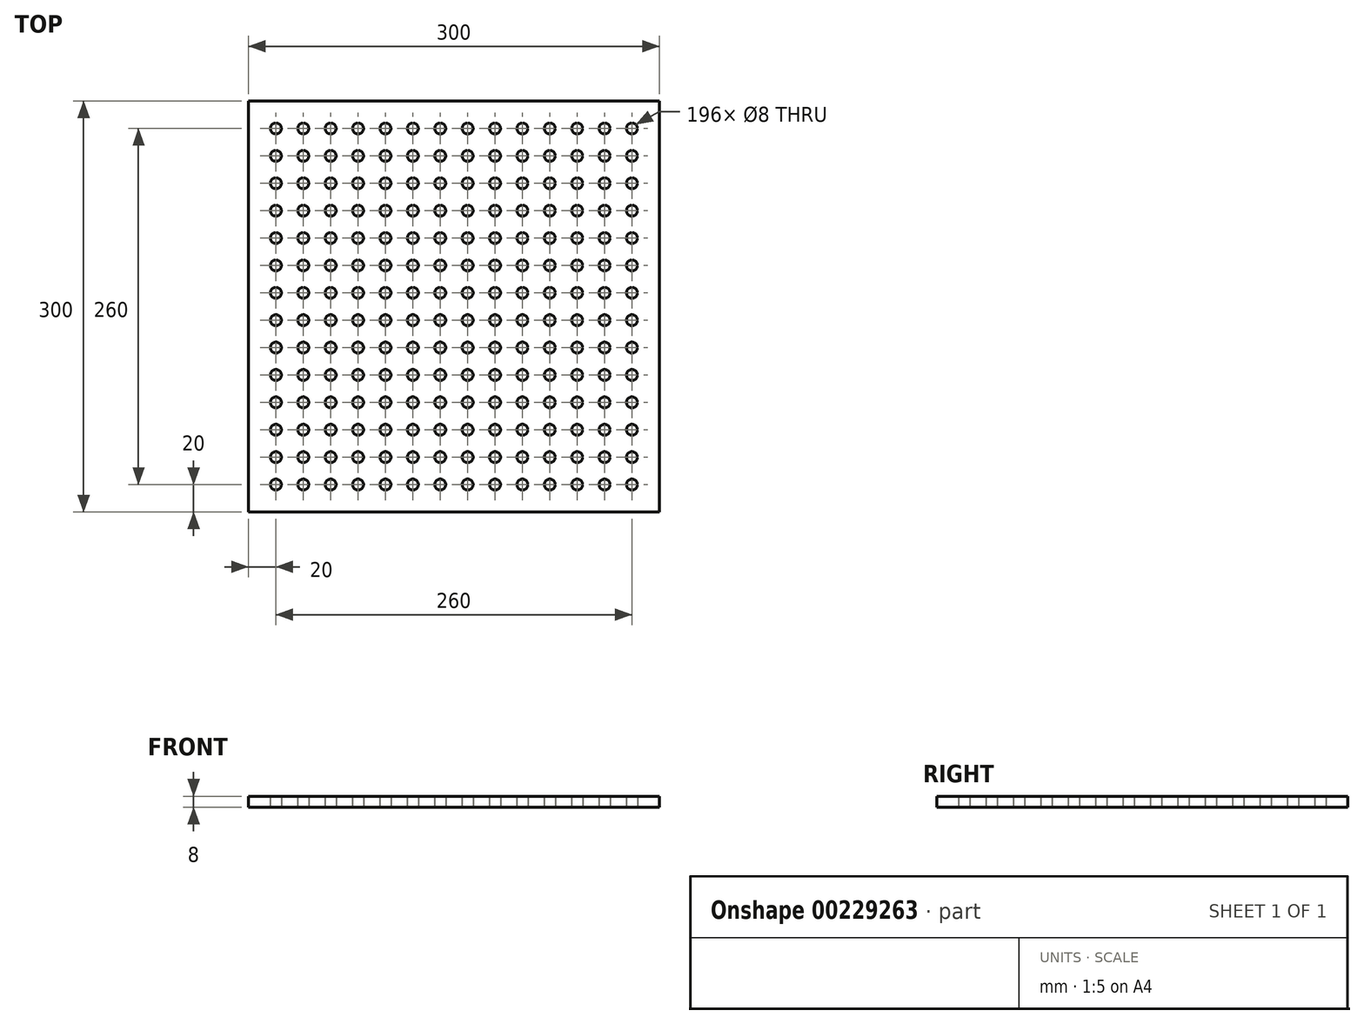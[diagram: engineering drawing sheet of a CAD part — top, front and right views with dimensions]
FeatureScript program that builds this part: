
annotation { "Feature Type Name" : "Feature", "Feature Type Description" : "" }
export const myFeature = defineFeature(function(context is Context, id is Id, definition is map)
    precondition{}
    {
        {
            var Q0;
            Q0=qCreatedBy(makeId("Top.planeOp"),FACE);
            var sketch = newSketch(context, id + "F0", { "sketchPlane" : qUnion([Q0])});
            skLineSegment(sketch, "E0.bottom", {"start": v(-150, 150) * mm, "end": v(150, 150) * mm});
            skLineSegment(sketch, "E0.top", {"start": v(-150, -150) * mm, "end": v(150, -150) * mm});
            skLineSegment(sketch, "E0.left", {"start": v(-150, 150) * mm, "end": v(-150, -150) * mm});
            skLineSegment(sketch, "E0.right", {"start": v(150, 150) * mm, "end": v(150, -150) * mm});
            skPoint(sketch, "E0.middle", {"position": v(0, 0) * mm});
            skCircle(sketch, "E1", {"center": v(-130, -130) * mm, "radius": 4 * mm});
            skCircle(sketch, "E2.0.1.0", {"center": v(-130, -110) * mm, "radius": 4 * mm});
            skCircle(sketch, "E2.0.2.0", {"center": v(-130, -90) * mm, "radius": 4 * mm});
            skCircle(sketch, "E2.0.3.0", {"center": v(-130, -70) * mm, "radius": 4 * mm});
            skCircle(sketch, "E2.0.4.0", {"center": v(-130, -50) * mm, "radius": 4 * mm});
            skCircle(sketch, "E2.0.5.0", {"center": v(-130, -30) * mm, "radius": 4 * mm});
            skCircle(sketch, "E2.0.6.0", {"center": v(-130, -10) * mm, "radius": 4 * mm});
            skCircle(sketch, "E2.0.7.0", {"center": v(-130, 10) * mm, "radius": 4 * mm});
            skCircle(sketch, "E2.0.8.0", {"center": v(-130, 30) * mm, "radius": 4 * mm});
            skCircle(sketch, "E2.0.9.0", {"center": v(-130, 50) * mm, "radius": 4 * mm});
            skCircle(sketch, "E2.0.10.0", {"center": v(-130, 70) * mm, "radius": 4 * mm});
            skCircle(sketch, "E2.0.11.0", {"center": v(-130, 90) * mm, "radius": 4 * mm});
            skCircle(sketch, "E2.0.12.0", {"center": v(-130, 110) * mm, "radius": 4 * mm});
            skCircle(sketch, "E2.0.13.0", {"center": v(-130, 130) * mm, "radius": 4 * mm});
            skCircle(sketch, "E2.1.0.0", {"center": v(-110, -130) * mm, "radius": 4 * mm});
            skCircle(sketch, "E2.1.1.0", {"center": v(-110, -110) * mm, "radius": 4 * mm});
            skCircle(sketch, "E2.1.2.0", {"center": v(-110, -90) * mm, "radius": 4 * mm});
            skCircle(sketch, "E2.1.3.0", {"center": v(-110, -70) * mm, "radius": 4 * mm});
            skCircle(sketch, "E2.1.4.0", {"center": v(-110, -50) * mm, "radius": 4 * mm});
            skCircle(sketch, "E2.1.5.0", {"center": v(-110, -30) * mm, "radius": 4 * mm});
            skCircle(sketch, "E2.1.6.0", {"center": v(-110, -10) * mm, "radius": 4 * mm});
            skCircle(sketch, "E2.1.7.0", {"center": v(-110, 10) * mm, "radius": 4 * mm});
            skCircle(sketch, "E2.1.8.0", {"center": v(-110, 30) * mm, "radius": 4 * mm});
            skCircle(sketch, "E2.1.9.0", {"center": v(-110, 50) * mm, "radius": 4 * mm});
            skCircle(sketch, "E2.1.10.0", {"center": v(-110, 70) * mm, "radius": 4 * mm});
            skCircle(sketch, "E2.1.11.0", {"center": v(-110, 90) * mm, "radius": 4 * mm});
            skCircle(sketch, "E2.1.12.0", {"center": v(-110, 110) * mm, "radius": 4 * mm});
            skCircle(sketch, "E2.1.13.0", {"center": v(-110, 130) * mm, "radius": 4 * mm});
            skCircle(sketch, "E2.2.0.0", {"center": v(-90, -130) * mm, "radius": 4 * mm});
            skCircle(sketch, "E2.2.1.0", {"center": v(-90, -110) * mm, "radius": 4 * mm});
            skCircle(sketch, "E2.2.2.0", {"center": v(-90, -90) * mm, "radius": 4 * mm});
            skCircle(sketch, "E2.2.3.0", {"center": v(-90, -70) * mm, "radius": 4 * mm});
            skCircle(sketch, "E2.2.4.0", {"center": v(-90, -50) * mm, "radius": 4 * mm});
            skCircle(sketch, "E2.2.5.0", {"center": v(-90, -30) * mm, "radius": 4 * mm});
            skCircle(sketch, "E2.2.6.0", {"center": v(-90, -10) * mm, "radius": 4 * mm});
            skCircle(sketch, "E2.2.7.0", {"center": v(-90, 10) * mm, "radius": 4 * mm});
            skCircle(sketch, "E2.2.8.0", {"center": v(-90, 30) * mm, "radius": 4 * mm});
            skCircle(sketch, "E2.2.9.0", {"center": v(-90, 50) * mm, "radius": 4 * mm});
            skCircle(sketch, "E2.2.10.0", {"center": v(-90, 70) * mm, "radius": 4 * mm});
            skCircle(sketch, "E2.2.11.0", {"center": v(-90, 90) * mm, "radius": 4 * mm});
            skCircle(sketch, "E2.2.12.0", {"center": v(-90, 110) * mm, "radius": 4 * mm});
            skCircle(sketch, "E2.2.13.0", {"center": v(-90, 130) * mm, "radius": 4 * mm});
            skCircle(sketch, "E2.3.0.0", {"center": v(-70, -130) * mm, "radius": 4 * mm});
            skCircle(sketch, "E2.3.1.0", {"center": v(-70, -110) * mm, "radius": 4 * mm});
            skCircle(sketch, "E2.3.2.0", {"center": v(-70, -90) * mm, "radius": 4 * mm});
            skCircle(sketch, "E2.3.3.0", {"center": v(-70, -70) * mm, "radius": 4 * mm});
            skCircle(sketch, "E2.3.4.0", {"center": v(-70, -50) * mm, "radius": 4 * mm});
            skCircle(sketch, "E2.3.5.0", {"center": v(-70, -30) * mm, "radius": 4 * mm});
            skCircle(sketch, "E2.3.6.0", {"center": v(-70, -10) * mm, "radius": 4 * mm});
            skCircle(sketch, "E2.3.7.0", {"center": v(-70, 10) * mm, "radius": 4 * mm});
            skCircle(sketch, "E2.3.8.0", {"center": v(-70, 30) * mm, "radius": 4 * mm});
            skCircle(sketch, "E2.3.9.0", {"center": v(-70, 50) * mm, "radius": 4 * mm});
            skCircle(sketch, "E2.3.10.0", {"center": v(-70, 70) * mm, "radius": 4 * mm});
            skCircle(sketch, "E2.3.11.0", {"center": v(-70, 90) * mm, "radius": 4 * mm});
            skCircle(sketch, "E2.3.12.0", {"center": v(-70, 110) * mm, "radius": 4 * mm});
            skCircle(sketch, "E2.3.13.0", {"center": v(-70, 130) * mm, "radius": 4 * mm});
            skCircle(sketch, "E2.4.0.0", {"center": v(-50, -130) * mm, "radius": 4 * mm});
            skCircle(sketch, "E2.4.1.0", {"center": v(-50, -110) * mm, "radius": 4 * mm});
            skCircle(sketch, "E2.4.2.0", {"center": v(-50, -90) * mm, "radius": 4 * mm});
            skCircle(sketch, "E2.4.3.0", {"center": v(-50, -70) * mm, "radius": 4 * mm});
            skCircle(sketch, "E2.4.4.0", {"center": v(-50, -50) * mm, "radius": 4 * mm});
            skCircle(sketch, "E2.4.5.0", {"center": v(-50, -30) * mm, "radius": 4 * mm});
            skCircle(sketch, "E2.4.6.0", {"center": v(-50, -10) * mm, "radius": 4 * mm});
            skCircle(sketch, "E2.4.7.0", {"center": v(-50, 10) * mm, "radius": 4 * mm});
            skCircle(sketch, "E2.4.8.0", {"center": v(-50, 30) * mm, "radius": 4 * mm});
            skCircle(sketch, "E2.4.9.0", {"center": v(-50, 50) * mm, "radius": 4 * mm});
            skCircle(sketch, "E2.4.10.0", {"center": v(-50, 70) * mm, "radius": 4 * mm});
            skCircle(sketch, "E2.4.11.0", {"center": v(-50, 90) * mm, "radius": 4 * mm});
            skCircle(sketch, "E2.4.12.0", {"center": v(-50, 110) * mm, "radius": 4 * mm});
            skCircle(sketch, "E2.4.13.0", {"center": v(-50, 130) * mm, "radius": 4 * mm});
            skCircle(sketch, "E2.5.0.0", {"center": v(-30, -130) * mm, "radius": 4 * mm});
            skCircle(sketch, "E2.5.1.0", {"center": v(-30, -110) * mm, "radius": 4 * mm});
            skCircle(sketch, "E2.5.2.0", {"center": v(-30, -90) * mm, "radius": 4 * mm});
            skCircle(sketch, "E2.5.3.0", {"center": v(-30, -70) * mm, "radius": 4 * mm});
            skCircle(sketch, "E2.5.4.0", {"center": v(-30, -50) * mm, "radius": 4 * mm});
            skCircle(sketch, "E2.5.5.0", {"center": v(-30, -30) * mm, "radius": 4 * mm});
            skCircle(sketch, "E2.5.6.0", {"center": v(-30, -10) * mm, "radius": 4 * mm});
            skCircle(sketch, "E2.5.7.0", {"center": v(-30, 10) * mm, "radius": 4 * mm});
            skCircle(sketch, "E2.5.8.0", {"center": v(-30, 30) * mm, "radius": 4 * mm});
            skCircle(sketch, "E2.5.9.0", {"center": v(-30, 50) * mm, "radius": 4 * mm});
            skCircle(sketch, "E2.5.10.0", {"center": v(-30, 70) * mm, "radius": 4 * mm});
            skCircle(sketch, "E2.5.11.0", {"center": v(-30, 90) * mm, "radius": 4 * mm});
            skCircle(sketch, "E2.5.12.0", {"center": v(-30, 110) * mm, "radius": 4 * mm});
            skCircle(sketch, "E2.5.13.0", {"center": v(-30, 130) * mm, "radius": 4 * mm});
            skCircle(sketch, "E2.6.0.0", {"center": v(-10, -130) * mm, "radius": 4 * mm});
            skCircle(sketch, "E2.6.1.0", {"center": v(-10, -110) * mm, "radius": 4 * mm});
            skCircle(sketch, "E2.6.2.0", {"center": v(-10, -90) * mm, "radius": 4 * mm});
            skCircle(sketch, "E2.6.3.0", {"center": v(-10, -70) * mm, "radius": 4 * mm});
            skCircle(sketch, "E2.6.4.0", {"center": v(-10, -50) * mm, "radius": 4 * mm});
            skCircle(sketch, "E2.6.5.0", {"center": v(-10, -30) * mm, "radius": 4 * mm});
            skCircle(sketch, "E2.6.6.0", {"center": v(-10, -10) * mm, "radius": 4 * mm});
            skCircle(sketch, "E2.6.7.0", {"center": v(-10, 10) * mm, "radius": 4 * mm});
            skCircle(sketch, "E2.6.8.0", {"center": v(-10, 30) * mm, "radius": 4 * mm});
            skCircle(sketch, "E2.6.9.0", {"center": v(-10, 50) * mm, "radius": 4 * mm});
            skCircle(sketch, "E2.6.10.0", {"center": v(-10, 70) * mm, "radius": 4 * mm});
            skCircle(sketch, "E2.6.11.0", {"center": v(-10, 90) * mm, "radius": 4 * mm});
            skCircle(sketch, "E2.6.12.0", {"center": v(-10, 110) * mm, "radius": 4 * mm});
            skCircle(sketch, "E2.6.13.0", {"center": v(-10, 130) * mm, "radius": 4 * mm});
            skCircle(sketch, "E2.7.0.0", {"center": v(10, -130) * mm, "radius": 4 * mm});
            skCircle(sketch, "E2.7.1.0", {"center": v(10, -110) * mm, "radius": 4 * mm});
            skCircle(sketch, "E2.7.2.0", {"center": v(10, -90) * mm, "radius": 4 * mm});
            skCircle(sketch, "E2.7.3.0", {"center": v(10, -70) * mm, "radius": 4 * mm});
            skCircle(sketch, "E2.7.4.0", {"center": v(10, -50) * mm, "radius": 4 * mm});
            skCircle(sketch, "E2.7.5.0", {"center": v(10, -30) * mm, "radius": 4 * mm});
            skCircle(sketch, "E2.7.6.0", {"center": v(10, -10) * mm, "radius": 4 * mm});
            skCircle(sketch, "E2.7.7.0", {"center": v(10, 10) * mm, "radius": 4 * mm});
            skCircle(sketch, "E2.7.8.0", {"center": v(10, 30) * mm, "radius": 4 * mm});
            skCircle(sketch, "E2.7.9.0", {"center": v(10, 50) * mm, "radius": 4 * mm});
            skCircle(sketch, "E2.7.10.0", {"center": v(10, 70) * mm, "radius": 4 * mm});
            skCircle(sketch, "E2.7.11.0", {"center": v(10, 90) * mm, "radius": 4 * mm});
            skCircle(sketch, "E2.7.12.0", {"center": v(10, 110) * mm, "radius": 4 * mm});
            skCircle(sketch, "E2.7.13.0", {"center": v(10, 130) * mm, "radius": 4 * mm});
            skCircle(sketch, "E2.8.0.0", {"center": v(30, -130) * mm, "radius": 4 * mm});
            skCircle(sketch, "E2.8.1.0", {"center": v(30, -110) * mm, "radius": 4 * mm});
            skCircle(sketch, "E2.8.2.0", {"center": v(30, -90) * mm, "radius": 4 * mm});
            skCircle(sketch, "E2.8.3.0", {"center": v(30, -70) * mm, "radius": 4 * mm});
            skCircle(sketch, "E2.8.4.0", {"center": v(30, -50) * mm, "radius": 4 * mm});
            skCircle(sketch, "E2.8.5.0", {"center": v(30, -30) * mm, "radius": 4 * mm});
            skCircle(sketch, "E2.8.6.0", {"center": v(30, -10) * mm, "radius": 4 * mm});
            skCircle(sketch, "E2.8.7.0", {"center": v(30, 10) * mm, "radius": 4 * mm});
            skCircle(sketch, "E2.8.8.0", {"center": v(30, 30) * mm, "radius": 4 * mm});
            skCircle(sketch, "E2.8.9.0", {"center": v(30, 50) * mm, "radius": 4 * mm});
            skCircle(sketch, "E2.8.10.0", {"center": v(30, 70) * mm, "radius": 4 * mm});
            skCircle(sketch, "E2.8.11.0", {"center": v(30, 90) * mm, "radius": 4 * mm});
            skCircle(sketch, "E2.8.12.0", {"center": v(30, 110) * mm, "radius": 4 * mm});
            skCircle(sketch, "E2.8.13.0", {"center": v(30, 130) * mm, "radius": 4 * mm});
            skCircle(sketch, "E2.9.0.0", {"center": v(50, -130) * mm, "radius": 4 * mm});
            skCircle(sketch, "E2.9.1.0", {"center": v(50, -110) * mm, "radius": 4 * mm});
            skCircle(sketch, "E2.9.2.0", {"center": v(50, -90) * mm, "radius": 4 * mm});
            skCircle(sketch, "E2.9.3.0", {"center": v(50, -70) * mm, "radius": 4 * mm});
            skCircle(sketch, "E2.9.4.0", {"center": v(50, -50) * mm, "radius": 4 * mm});
            skCircle(sketch, "E2.9.5.0", {"center": v(50, -30) * mm, "radius": 4 * mm});
            skCircle(sketch, "E2.9.6.0", {"center": v(50, -10) * mm, "radius": 4 * mm});
            skCircle(sketch, "E2.9.7.0", {"center": v(50, 10) * mm, "radius": 4 * mm});
            skCircle(sketch, "E2.9.8.0", {"center": v(50, 30) * mm, "radius": 4 * mm});
            skCircle(sketch, "E2.9.9.0", {"center": v(50, 50) * mm, "radius": 4 * mm});
            skCircle(sketch, "E2.9.10.0", {"center": v(50, 70) * mm, "radius": 4 * mm});
            skCircle(sketch, "E2.9.11.0", {"center": v(50, 90) * mm, "radius": 4 * mm});
            skCircle(sketch, "E2.9.12.0", {"center": v(50, 110) * mm, "radius": 4 * mm});
            skCircle(sketch, "E2.9.13.0", {"center": v(50, 130) * mm, "radius": 4 * mm});
            skCircle(sketch, "E2.10.0.0", {"center": v(70, -130) * mm, "radius": 4 * mm});
            skCircle(sketch, "E2.10.1.0", {"center": v(70, -110) * mm, "radius": 4 * mm});
            skCircle(sketch, "E2.10.2.0", {"center": v(70, -90) * mm, "radius": 4 * mm});
            skCircle(sketch, "E2.10.3.0", {"center": v(70, -70) * mm, "radius": 4 * mm});
            skCircle(sketch, "E2.10.4.0", {"center": v(70, -50) * mm, "radius": 4 * mm});
            skCircle(sketch, "E2.10.5.0", {"center": v(70, -30) * mm, "radius": 4 * mm});
            skCircle(sketch, "E2.10.6.0", {"center": v(70, -10) * mm, "radius": 4 * mm});
            skCircle(sketch, "E2.10.7.0", {"center": v(70, 10) * mm, "radius": 4 * mm});
            skCircle(sketch, "E2.10.8.0", {"center": v(70, 30) * mm, "radius": 4 * mm});
            skCircle(sketch, "E2.10.9.0", {"center": v(70, 50) * mm, "radius": 4 * mm});
            skCircle(sketch, "E2.10.10.0", {"center": v(70, 70) * mm, "radius": 4 * mm});
            skCircle(sketch, "E2.10.11.0", {"center": v(70, 90) * mm, "radius": 4 * mm});
            skCircle(sketch, "E2.10.12.0", {"center": v(70, 110) * mm, "radius": 4 * mm});
            skCircle(sketch, "E2.10.13.0", {"center": v(70, 130) * mm, "radius": 4 * mm});
            skCircle(sketch, "E2.11.0.0", {"center": v(90, -130) * mm, "radius": 4 * mm});
            skCircle(sketch, "E2.11.1.0", {"center": v(90, -110) * mm, "radius": 4 * mm});
            skCircle(sketch, "E2.11.2.0", {"center": v(90, -90) * mm, "radius": 4 * mm});
            skCircle(sketch, "E2.11.3.0", {"center": v(90, -70) * mm, "radius": 4 * mm});
            skCircle(sketch, "E2.11.4.0", {"center": v(90, -50) * mm, "radius": 4 * mm});
            skCircle(sketch, "E2.11.5.0", {"center": v(90, -30) * mm, "radius": 4 * mm});
            skCircle(sketch, "E2.11.6.0", {"center": v(90, -10) * mm, "radius": 4 * mm});
            skCircle(sketch, "E2.11.7.0", {"center": v(90, 10) * mm, "radius": 4 * mm});
            skCircle(sketch, "E2.11.8.0", {"center": v(90, 30) * mm, "radius": 4 * mm});
            skCircle(sketch, "E2.11.9.0", {"center": v(90, 50) * mm, "radius": 4 * mm});
            skCircle(sketch, "E2.11.10.0", {"center": v(90, 70) * mm, "radius": 4 * mm});
            skCircle(sketch, "E2.11.11.0", {"center": v(90, 90) * mm, "radius": 4 * mm});
            skCircle(sketch, "E2.11.12.0", {"center": v(90, 110) * mm, "radius": 4 * mm});
            skCircle(sketch, "E2.11.13.0", {"center": v(90, 130) * mm, "radius": 4 * mm});
            skCircle(sketch, "E2.12.0.0", {"center": v(110, -130) * mm, "radius": 4 * mm});
            skCircle(sketch, "E2.12.1.0", {"center": v(110, -110) * mm, "radius": 4 * mm});
            skCircle(sketch, "E2.12.2.0", {"center": v(110, -90) * mm, "radius": 4 * mm});
            skCircle(sketch, "E2.12.3.0", {"center": v(110, -70) * mm, "radius": 4 * mm});
            skCircle(sketch, "E2.12.4.0", {"center": v(110, -50) * mm, "radius": 4 * mm});
            skCircle(sketch, "E2.12.5.0", {"center": v(110, -30) * mm, "radius": 4 * mm});
            skCircle(sketch, "E2.12.6.0", {"center": v(110, -10) * mm, "radius": 4 * mm});
            skCircle(sketch, "E2.12.7.0", {"center": v(110, 10) * mm, "radius": 4 * mm});
            skCircle(sketch, "E2.12.8.0", {"center": v(110, 30) * mm, "radius": 4 * mm});
            skCircle(sketch, "E2.12.9.0", {"center": v(110, 50) * mm, "radius": 4 * mm});
            skCircle(sketch, "E2.12.10.0", {"center": v(110, 70) * mm, "radius": 4 * mm});
            skCircle(sketch, "E2.12.11.0", {"center": v(110, 90) * mm, "radius": 4 * mm});
            skCircle(sketch, "E2.12.12.0", {"center": v(110, 110) * mm, "radius": 4 * mm});
            skCircle(sketch, "E2.12.13.0", {"center": v(110, 130) * mm, "radius": 4 * mm});
            skCircle(sketch, "E2.13.0.0", {"center": v(130, -130) * mm, "radius": 4 * mm});
            skCircle(sketch, "E2.13.1.0", {"center": v(130, -110) * mm, "radius": 4 * mm});
            skCircle(sketch, "E2.13.2.0", {"center": v(130, -90) * mm, "radius": 4 * mm});
            skCircle(sketch, "E2.13.3.0", {"center": v(130, -70) * mm, "radius": 4 * mm});
            skCircle(sketch, "E2.13.4.0", {"center": v(130, -50) * mm, "radius": 4 * mm});
            skCircle(sketch, "E2.13.5.0", {"center": v(130, -30) * mm, "radius": 4 * mm});
            skCircle(sketch, "E2.13.6.0", {"center": v(130, -10) * mm, "radius": 4 * mm});
            skCircle(sketch, "E2.13.7.0", {"center": v(130, 10) * mm, "radius": 4 * mm});
            skCircle(sketch, "E2.13.8.0", {"center": v(130, 30) * mm, "radius": 4 * mm});
            skCircle(sketch, "E2.13.9.0", {"center": v(130, 50) * mm, "radius": 4 * mm});
            skCircle(sketch, "E2.13.10.0", {"center": v(130, 70) * mm, "radius": 4 * mm});
            skCircle(sketch, "E2.13.11.0", {"center": v(130, 90) * mm, "radius": 4 * mm});
            skCircle(sketch, "E2.13.12.0", {"center": v(130, 110) * mm, "radius": 4 * mm});
            skCircle(sketch, "E2.13.13.0", {"center": v(130, 130) * mm, "radius": 4 * mm});
            skLineSegment(sketch, "E2.direction1", {"start": v(-130, -130) * mm, "end": v(-110, -130) * mm, "construction": true});
            skLineSegment(sketch, "E2.direction2", {"start": v(-130, -130) * mm, "end": v(-130, -110) * mm, "construction": true});
            skSolve(sketch);
        }
        {
            var Q0;
            Q0=makeQuery(id+"F0.imprint","IMPRINT",FACE,{"disambiguationData":[TD([[makeQuery(id+"F0.imprint","IMPRINT",EDGE,{"derivedFrom":sQuery(id+"F0.wireOp",EDGE,"E0.bottom")}),-1.0]])]});
            extrude(context, id + "F1", {"entities" : qUnion([Q0]), "depth" : 8 * mm});
        }
    });
